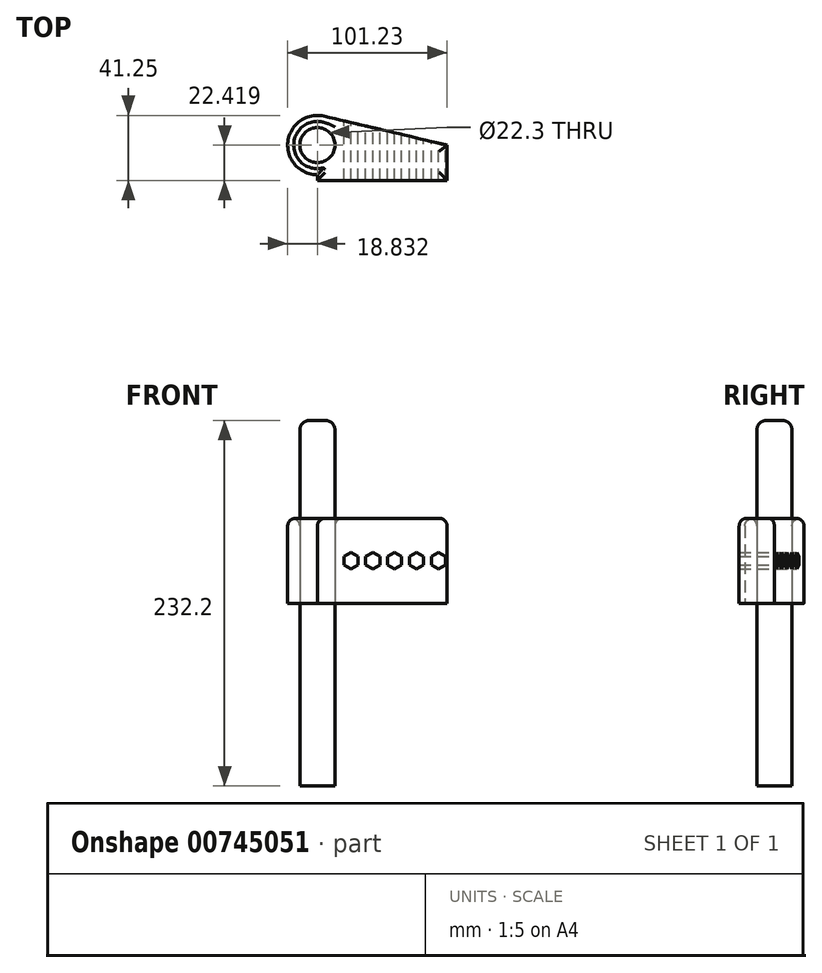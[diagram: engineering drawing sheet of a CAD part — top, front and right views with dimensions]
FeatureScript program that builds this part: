
annotation { "Feature Type Name" : "Feature", "Feature Type Description" : "" }
export const myFeature = defineFeature(function(context is Context, id is Id, definition is map)
    precondition{}
    {
        {
            var Q0;
            Q0=qCreatedBy(makeId("Top.planeOp"),FACE);
            var sketch = newSketch(context, id + "F0", { "sketchPlane" : qUnion([Q0])});
            skLineSegment(sketch, "E0.bottom", {"start": v(41.2, 11.2) * mm, "end": v(-41.2, 11.2) * mm});
            skLineSegment(sketch, "E0.top", {"start": v(41.2, -11.2) * mm, "end": v(-41.2, -11.2) * mm});
            skLineSegment(sketch, "E0.left", {"start": v(41.2, 11.2) * mm, "end": v(41.2, -11.2) * mm});
            skLineSegment(sketch, "E0.right", {"start": v(-41.2, 11.2) * mm, "end": v(-41.2, -11.2) * mm});
            skPoint(sketch, "E0.middle", {"position": v(0, 0) * mm});
            skCircle(sketch, "E1", {"center": v(-41.2, 11.2) * mm, "radius": 11.15 * mm});
            skCircle(sketch, "E2", {"center": v(-41.2, 11.2) * mm, "radius": 18.83 * mm});
            skFitSpline(sketch, "E3", {"points": [v(41.2, 11.2) * mm, v(-36.9, 29.54) * mm], "startDerivative": vector(-78.1, 18.34) * mm, "endDerivative": vector(-78.1, 18.34) * mm});
            skFitSpline(sketch, "E4", {"points": [v(41.2, 11.2) * mm, v(0, 11.2) * mm], "startDerivative": vector(-41.2, 0) * mm, "endDerivative": vector(-41.2, 0) * mm});
            skSolve(sketch);
        }
        {
            var Q0;
            Q0 = qSketchRegion(id + "F0", true);
            extrude(context, id + "F1", {"entities" : qUnion([Q0]), "depth" : 54 * mm, "offsetDistance" : 25 * mm});
        }
        {
            var Q0;
            {var subQ0=sQuery(id+"F0.wireOp",EDGE,"E0.right");var subQ1=sQuery(id+"F0.wireOp",EDGE,"E0.bottom");var subQ2=makeQuery(id+"F0.imprint","INTERSECT",VERTEX,{"derivedFrom":[subQ1,subQ0]});Q0=makeQuery(id+"F0.imprint","IMPRINT",FACE,{"disambiguationData":[TD([[makeQuery(id+"F0.imprint","IMPRINT",EDGE,{"disambiguationData":[TD([[subQ2,1.0]])],"derivedFrom":subQ1}),1.0]])]});}
            var Q1;
            {var subQ0=sQuery(id+"F0.wireOp",EDGE,"E0.right");var subQ1=sQuery(id+"F0.wireOp",EDGE,"E0.bottom");var subQ2=makeQuery(id+"F0.imprint","INTERSECT",VERTEX,{"derivedFrom":[subQ1,subQ0]});Q1=makeQuery(id+"F0.imprint","IMPRINT",FACE,{"disambiguationData":[TD([[makeQuery(id+"F0.imprint","IMPRINT",EDGE,{"disambiguationData":[TD([[subQ2,1.0]])],"derivedFrom":subQ1}),-1.0]])]});}
            extrude(context, id + "F2", {"entities" : qUnion([Q0, Q1]), "endBound" : BoundingType.SYMMETRIC, "depth" : 232.2 * mm, "offsetDistance" : 25 * mm});
        }
        {
            var Q0;
            Q0=makeQuery(id+"F1.opExtrude","SWEPT_FACE",FACE,{"disambiguationData":[OSD([sQuery(id+"F0.wireOp",EDGE,"E0.top")])]});
            var sketch = newSketch(context, id + "F3", { "sketchPlane" : qUnion([Q0])});
            skCircle(sketch, "E5.cCircle", {"center": v(-19.9, 27) * mm, "radius": 4.49 * mm, "construction": true});
            skPoint(sketch, "E5.cCircle.centerSnap0", {"position": v(-41.2, 27) * mm});
            skLineSegment(sketch, "E5.0", {"start": v(-15.4, 29.6) * mm, "end": v(-15.4, 24.4) * mm});
            skLineSegment(sketch, "E5.1", {"start": v(-15.4, 24.4) * mm, "end": v(-19.9, 21.82) * mm});
            skLineSegment(sketch, "E5.2", {"start": v(-19.9, 21.82) * mm, "end": v(-24.38, 24.4) * mm});
            skLineSegment(sketch, "E5.3", {"start": v(-24.38, 24.4) * mm, "end": v(-24.38, 29.6) * mm});
            skLineSegment(sketch, "E5.4", {"start": v(-24.38, 29.6) * mm, "end": v(-19.9, 32.18) * mm});
            skLineSegment(sketch, "E5.5", {"start": v(-19.9, 32.18) * mm, "end": v(-15.4, 29.6) * mm});
            skLineSegment(sketch, "E6.1.0.0", {"start": v(-6, 32.18) * mm, "end": v(-1.5, 29.6) * mm});
            skLineSegment(sketch, "E6.1.0.1", {"start": v(-10.48, 29.6) * mm, "end": v(-6, 32.18) * mm});
            skLineSegment(sketch, "E6.1.0.2", {"start": v(-10.48, 24.4) * mm, "end": v(-10.48, 29.6) * mm});
            skLineSegment(sketch, "E6.1.0.3", {"start": v(-6, 21.82) * mm, "end": v(-10.48, 24.4) * mm});
            skLineSegment(sketch, "E6.1.0.4", {"start": v(-1.5, 24.4) * mm, "end": v(-6, 21.82) * mm});
            skCircle(sketch, "E6.1.0.5", {"center": v(-6, 27) * mm, "radius": 4.49 * mm, "construction": true});
            skLineSegment(sketch, "E6.1.0.6", {"start": v(-1.5, 29.6) * mm, "end": v(-1.5, 24.4) * mm});
            skLineSegment(sketch, "E6.2.0.0", {"start": v(7.9, 32.18) * mm, "end": v(12.4, 29.6) * mm});
            skLineSegment(sketch, "E6.2.0.1", {"start": v(3.42, 29.6) * mm, "end": v(7.9, 32.18) * mm});
            skLineSegment(sketch, "E6.2.0.2", {"start": v(3.42, 24.4) * mm, "end": v(3.42, 29.6) * mm});
            skLineSegment(sketch, "E6.2.0.3", {"start": v(7.9, 21.82) * mm, "end": v(3.42, 24.4) * mm});
            skLineSegment(sketch, "E6.2.0.4", {"start": v(12.4, 24.4) * mm, "end": v(7.9, 21.82) * mm});
            skCircle(sketch, "E6.2.0.5", {"center": v(7.9, 27) * mm, "radius": 4.49 * mm, "construction": true});
            skLineSegment(sketch, "E6.2.0.6", {"start": v(12.4, 29.6) * mm, "end": v(12.4, 24.4) * mm});
            skLineSegment(sketch, "E6.3.0.0", {"start": v(21.8, 32.18) * mm, "end": v(26.3, 29.6) * mm});
            skLineSegment(sketch, "E6.3.0.1", {"start": v(17.32, 29.6) * mm, "end": v(21.8, 32.18) * mm});
            skLineSegment(sketch, "E6.3.0.2", {"start": v(17.32, 24.4) * mm, "end": v(17.32, 29.6) * mm});
            skLineSegment(sketch, "E6.3.0.3", {"start": v(21.8, 21.82) * mm, "end": v(17.32, 24.4) * mm});
            skLineSegment(sketch, "E6.3.0.4", {"start": v(26.3, 24.4) * mm, "end": v(21.8, 21.82) * mm});
            skCircle(sketch, "E6.3.0.5", {"center": v(21.8, 27) * mm, "radius": 4.49 * mm, "construction": true});
            skLineSegment(sketch, "E6.3.0.6", {"start": v(26.3, 29.6) * mm, "end": v(26.3, 24.4) * mm});
            skLineSegment(sketch, "E6.4.0.0", {"start": v(35.7, 32.18) * mm, "end": v(40.2, 29.6) * mm});
            skLineSegment(sketch, "E6.4.0.1", {"start": v(31.22, 29.6) * mm, "end": v(35.7, 32.18) * mm});
            skLineSegment(sketch, "E6.4.0.2", {"start": v(31.22, 24.4) * mm, "end": v(31.22, 29.6) * mm});
            skLineSegment(sketch, "E6.4.0.3", {"start": v(35.7, 21.82) * mm, "end": v(31.22, 24.4) * mm});
            skLineSegment(sketch, "E6.4.0.4", {"start": v(40.2, 24.4) * mm, "end": v(35.7, 21.82) * mm});
            skCircle(sketch, "E6.4.0.5", {"center": v(35.7, 27) * mm, "radius": 4.49 * mm, "construction": true});
            skLineSegment(sketch, "E6.4.0.6", {"start": v(40.2, 29.6) * mm, "end": v(40.2, 24.4) * mm});
            skLineSegment(sketch, "E6.direction1", {"start": v(-24.38, 24.4) * mm, "end": v(-10.48, 24.4) * mm, "construction": true});
            skSolve(sketch);
        }
        {
            var Q0;
            Q0=makeQuery(id+"F3.imprint","IMPRINT",FACE,{"disambiguationData":[TD([[makeQuery(id+"F3.imprint","IMPRINT",EDGE,{"derivedFrom":sQuery(id+"F3.wireOp",EDGE,"E5.0")}),-1.0]])]});
            var Q1;
            Q1=makeQuery(id+"F3.imprint","IMPRINT",FACE,{"disambiguationData":[TD([[makeQuery(id+"F3.imprint","IMPRINT",EDGE,{"derivedFrom":sQuery(id+"F3.wireOp",EDGE,"E6.1.0.0")}),-1.0]])]});
            var Q2;
            Q2=makeQuery(id+"F3.imprint","IMPRINT",FACE,{"disambiguationData":[TD([[makeQuery(id+"F3.imprint","IMPRINT",EDGE,{"derivedFrom":sQuery(id+"F3.wireOp",EDGE,"E6.2.0.0")}),-1.0]])]});
            var Q3;
            Q3=makeQuery(id+"F3.imprint","IMPRINT",FACE,{"disambiguationData":[TD([[makeQuery(id+"F3.imprint","IMPRINT",EDGE,{"derivedFrom":sQuery(id+"F3.wireOp",EDGE,"E6.3.0.0")}),-1.0]])]});
            var Q4;
            Q4=makeQuery(id+"F3.imprint","IMPRINT",FACE,{"disambiguationData":[TD([[makeQuery(id+"F3.imprint","IMPRINT",EDGE,{"derivedFrom":sQuery(id+"F3.wireOp",EDGE,"E6.4.0.0")}),-1.0]])]});
            extrude(context, id + "F4", {"entities" : qUnion([Q0, Q1, Q2, Q3, Q4]), "operationType" : NewBodyOperationType.REMOVE, "endBound" : BoundingType.THROUGH_ALL, "depth" : 25 * mm, "offsetDistance" : 25 * mm, "hasSecondDirection" : true, "secondDirectionOppositeDirection" : true, "secondDirectionDepth" : 304 * mm});
        }
        {
            var Q0;
            Q0=makeQuery(id+"F1.opExtrude","CAP_FACE",FACE,{"disambiguationData":[OSD([sQuery(id+"F0.wireOp",EDGE,"E0.top"),sQuery(id+"F0.wireOp",EDGE,"E0.left"),sQuery(id+"F0.wireOp",EDGE,"E0.right"),sQuery(id+"F0.wireOp",EDGE,"E1"),sQuery(id+"F0.wireOp",EDGE,"E2"),sQuery(id+"F0.wireOp",EDGE,"E3")])],"isStart":false});
            fillet(context, id + "F5", {"entities" : qUnion([Q0]), "radius" : 5 * mm, "tangentPropagation" : true, "allowEdgeOverflow" : false});
        }
        {
            var Q0;
            Q0=makeQuery(id+"F2.opExtrude","CAP_EDGE",EDGE,{"disambiguationData":[OSD([sQuery(id+"F0.wireOp",EDGE,"E1")])],"isStart":false});
            fillet(context, id + "F6", {"entities" : qUnion([Q0]), "radius" : 6 * mm, "tangentPropagation" : true, "allowEdgeOverflow" : false});
        }
    });
